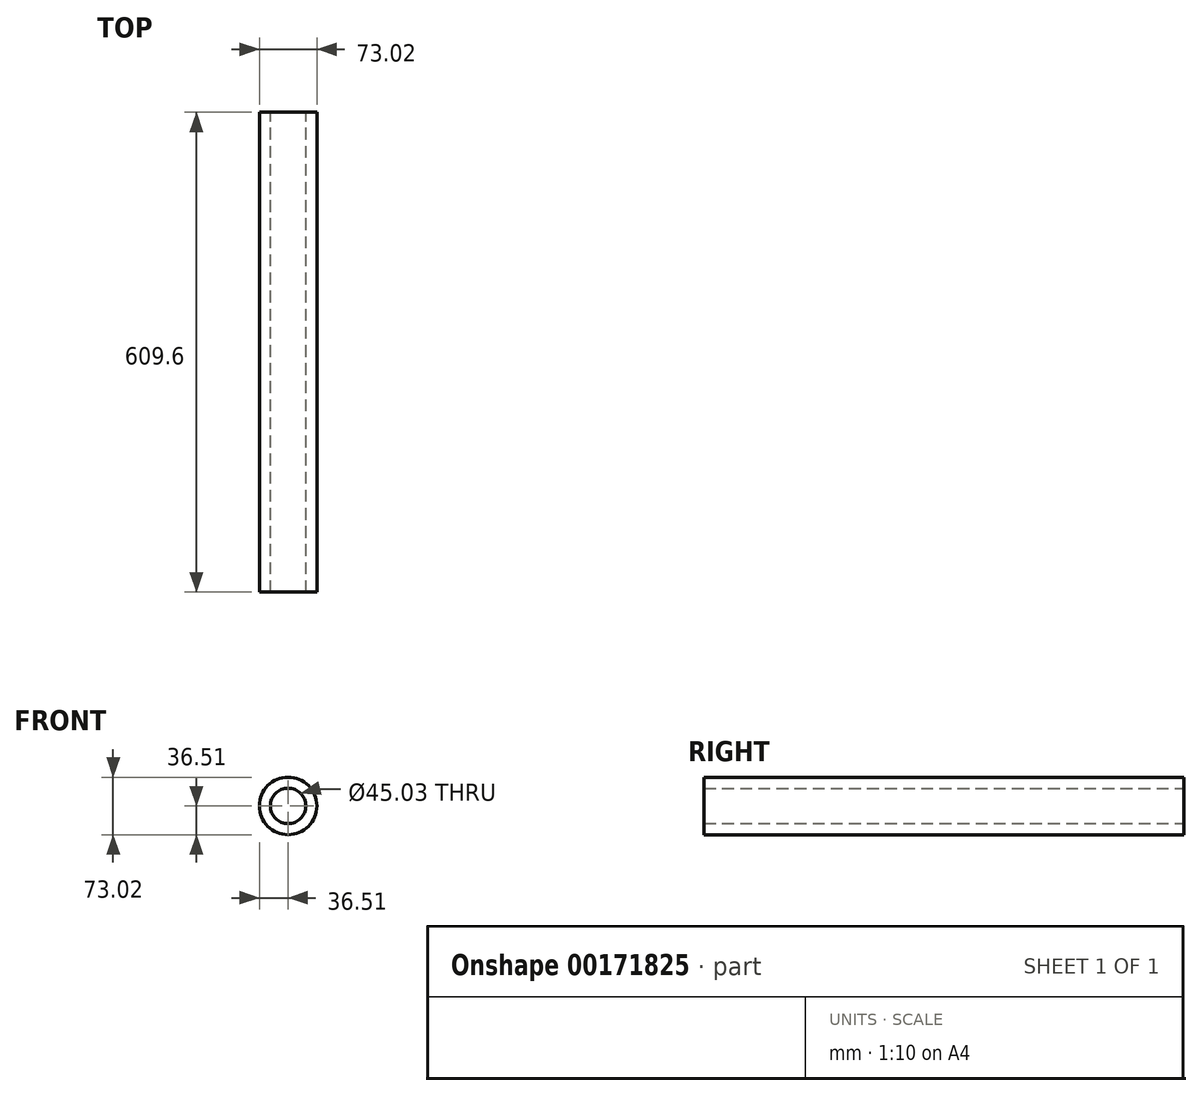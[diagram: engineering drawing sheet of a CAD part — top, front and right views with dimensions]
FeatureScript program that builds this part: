
annotation { "Feature Type Name" : "Feature", "Feature Type Description" : "" }
export const myFeature = defineFeature(function(context is Context, id is Id, definition is map)
    precondition{}
    {
        {
            var Q0;
            Q0=qCreatedBy(makeId("Front.planeOp"),FACE);
            var sketch = newSketch(context, id + "F0", { "sketchPlane" : qUnion([Q0])});
            skCircle(sketch, "E0", {"center": v(0, 0) * mm, "radius": 36.51 * mm});
            skCircle(sketch, "E1", {"center": v(0, 0) * mm, "radius": 22.52 * mm});
            skSolve(sketch);
        }
        {
            var Q0;
            Q0=makeQuery(id+"F0.imprint","IMPRINT",FACE,{"disambiguationData":[TD([[makeQuery(id+"F0.imprint","IMPRINT",EDGE,{"derivedFrom":sQuery(id+"F0.wireOp",EDGE,"E0")}),1.0]])]});
            extrude(context, id + "F1", {"entities" : qUnion([Q0]), "endBound" : BoundingType.SYMMETRIC, "depth" : 609.6 * mm});
        }
    });
